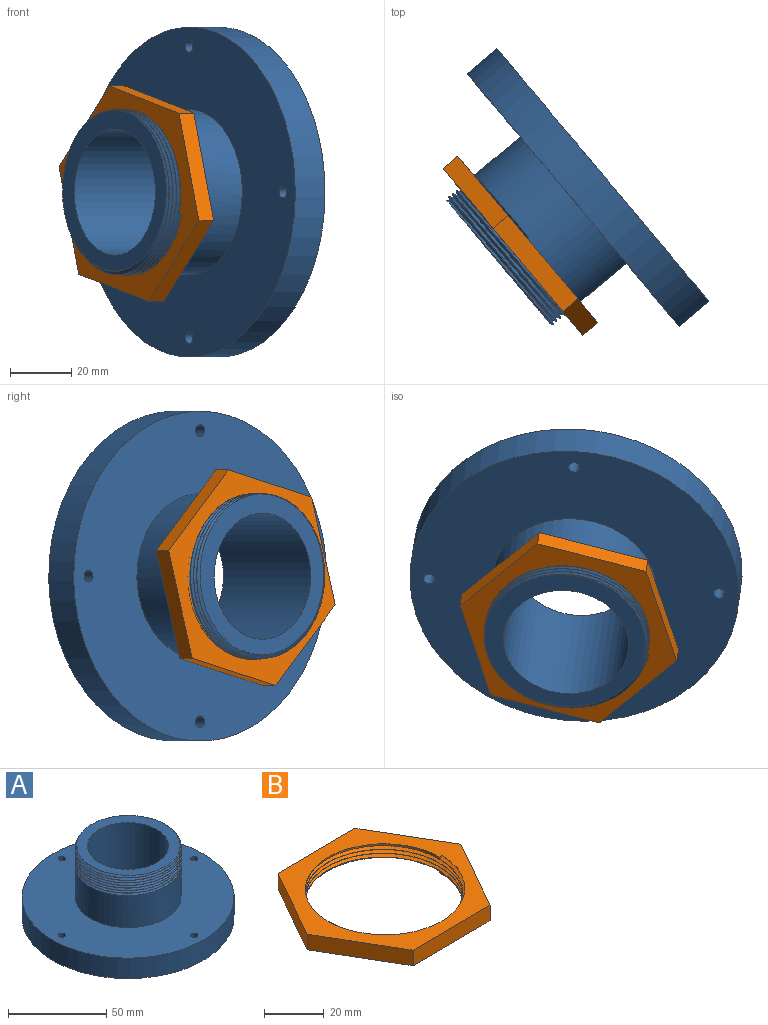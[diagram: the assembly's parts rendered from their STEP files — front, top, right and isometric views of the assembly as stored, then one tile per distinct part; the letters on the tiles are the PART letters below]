
ASSEMBLY  parts=2 mates=1
PART A: 22 faces, bbox 108.9x108.9x46.3 mm
  f0: cylinder r=26.99mm len=53.98mm, axis (0,0,-1), area 3351.7mm2, adj f8,f15,f18,f20
  f1: cylinder r=26.99mm len=18.74mm, axis (0,0,-1), area 2.1mm2, adj f2,f9,f19,f21
  f2: cylinder r=26.99mm len=53.98mm, axis (0,0,-1), area 20mm2, adj f1,f3,f20,f21
  f3: cylinder r=26.99mm len=53.98mm, axis (0,0,-1), area 20.2mm2, adj f2,f4,f20,f21
  f4: cylinder r=26.99mm len=53.98mm, axis (0,0,-1), area 20.2mm2, adj f3,f5,f20,f21
  f5: cylinder r=26.99mm len=53.98mm, axis (0,0,-1), area 20.2mm2, adj f4,f6,f20,f21
  f6: cylinder r=26.99mm len=53.98mm, axis (0,0,-1), area 20mm2, adj f5,f7,f20,f21
  f7: cylinder r=26.99mm len=53.98mm, axis (0,0,-1), area 20.2mm2, adj f6,f8,f20,f21
  f8: cylinder r=26.99mm len=53.98mm, axis (0,0,-1), area 20.2mm2, adj f0,f7,f20,f21
  f9: plane 53.89x53.76mm, normal (0,0,1), area 852.5mm2, adj f1,f17,f19,f20,f21
  f10: cylinder r=1.9mm len=12.7mm, axis (0,0,-1), area 151.6mm2, adj f15,f16
  f11: cylinder r=1.9mm len=12.7mm, axis (0,0,-1), area 151.6mm2, adj f15,f16
  f12: cylinder r=1.9mm len=12.7mm, axis (0,0,-1), area 151.6mm2, adj f15,f16
  f13: cylinder r=1.9mm len=12.7mm, axis (0,0,-1), area 151.6mm2, adj f15,f16
  f14: cylinder r=53.98mm len=107.95mm, axis (0,0,-1), area 4307mm2, adj f15,f16
  f15: plane 107.95x107.95mm, normal (0,0,1), area 6818.9mm2, adj f0,f10,f11,f12,f13,f14
  f16: plane 107.95x107.95mm, normal (0,0,-1), area 7769mm2, adj f10,f11,f12,f13,f14,f17
  f17: cylinder r=20.64mm len=44.45mm, axis (0,0,-1), area 5763.8mm2, adj f9,f16
  f18: plane 1.47x1.27mm, normal (0,1,0), area 0.9mm2, adj f0,f20,f21
  f19: plane 0.13x0.08mm, normal (0,-1,0), area 0mm2, adj f1,f9,f20
  f20: bspline ~62.39x54.03mm, area 1900.7mm2, adj f0,f2,f3,f4,f5,f6,f7,f8
  f21: bspline ~62.39x54.03mm, area 1789.3mm2, adj f1,f2,f3,f4,f5,f6,f7,f8
PART B: 13 faces, bbox 73.3x63.8x7.9 mm
  f0: plane 73.32x63.73mm, normal (0,0,-1), area 1247.3mm2, adj f1,f2,f3,f4,f5,f6,f7,f9
  f1: plane 31.87x18.13mm, normal (0.87,-0.49,0), area 232.8mm2, adj f0,f2,f6,f8
  f2: plane 31.63x18.53mm, normal (0.86,0.51,0), area 232.8mm2, adj f0,f1,f3,f8
  f3: plane 36.66x6.35mm, normal (-0.01,1,0), area 232.8mm2, adj f0,f2,f4,f8
  f4: plane 31.87x18.13mm, normal (-0.87,0.49,0), area 232.8mm2, adj f0,f3,f5,f8
  f5: plane 31.63x18.53mm, normal (-0.86,-0.51,0), area 232.8mm2, adj f0,f4,f6,f8
  f6: plane 36.66x6.35mm, normal (0.01,-1,0), area 232.8mm2, adj f0,f1,f5,f8
  f7: cylinder r=26.34mm len=52.68mm, axis (0,0,-1), area 133.8mm2, adj f0,f8,f9,f10,f11,f12
  f8: plane 73.32x63.73mm, normal (0,0,1), area 1278.8mm2, adj f1,f2,f3,f4,f5,f6,f7,f9
  f9: bspline ~63.77x55.23mm, area 959.4mm2, adj f0,f7,f8,f10,f11,f12
  f10: plane 1.06x0.61mm, normal (0,1,0), area 0.3mm2, adj f0,f7,f9
  f11: plane 1.28x0.86mm, normal (0,-1,0), area 0.6mm2, adj f7,f8,f9,f12
  f12: bspline ~63.77x55.23mm, area 921.4mm2, adj f0,f7,f9,f11
PLACE A rot(axis=(0.32,-0.89,0.32),96.7deg) t=(-74.01,9.68,15.1)mm
PLACE B rot(axis=(0.84,-0.27,-0.47),106.5deg) t=(-98.59,-11.35,14.58)mm
MATE cylindrical B.f8 <-> A.f14  axis (-0.77,-0.64,0) through (-103.65,-15.2,15.1)mm
